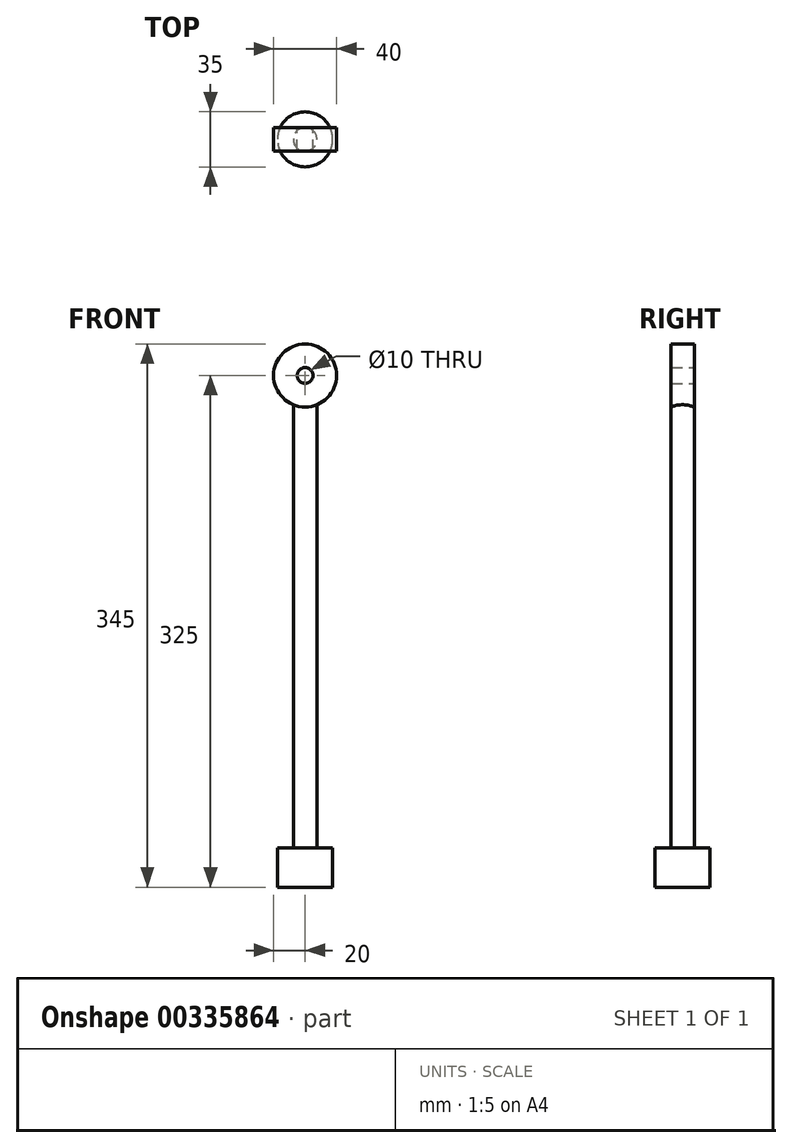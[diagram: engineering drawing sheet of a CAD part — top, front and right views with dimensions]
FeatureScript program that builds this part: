
annotation { "Feature Type Name" : "Feature", "Feature Type Description" : "" }
export const myFeature = defineFeature(function(context is Context, id is Id, definition is map)
    precondition{}
    {
        {
            var Q0;
            Q0=qCreatedBy(makeId("Front.planeOp"),FACE);
            var sketch = newSketch(context, id + "F0", { "sketchPlane" : qUnion([Q0])});
            skCircle(sketch, "E0", {"center": v(0, 0) * mm, "radius": 20 * mm});
            skCircle(sketch, "E1", {"center": v(0, 0) * mm, "radius": 5 * mm});
            skSolve(sketch);
        }
        {
            var Q0;
            Q0=makeQuery(id+"F0.imprint","IMPRINT",FACE,{"disambiguationData":[TD([[makeQuery(id+"F0.imprint","IMPRINT",EDGE,{"derivedFrom":sQuery(id+"F0.wireOp",EDGE,"E0")}),1.0]])]});
            extrude(context, id + "F1", {"entities" : qUnion([Q0]), "depth" : 15 * mm, "symmetric" : true});
        }
        {
            var Q0;
            Q0=qCreatedBy(makeId("Top.planeOp"),FACE);
            cPlane(context, id + "F2", {"entities" : qUnion([Q0]), "cplaneType" : CPlaneType.OFFSET, "offset" : 300 * mm, "oppositeDirection" : true, "width" : 150 * mm, "height" : 150 * mm});
        }
        {
            var Q0;
            Q0=qCreatedBy(id+"F2.planeOp",FACE);
            var sketch = newSketch(context, id + "F3", { "sketchPlane" : qUnion([Q0])});
            skCircle(sketch, "E2", {"center": v(0, 0) * mm, "radius": 7.5 * mm});
            skSolve(sketch);
        }
        {
            var Q0;
            Q0=makeQuery(id+"F3.imprint","IMPRINT",FACE,{"disambiguationData":[TD([[makeQuery(id+"F3.imprint","IMPRINT",EDGE,{"derivedFrom":sQuery(id+"F3.wireOp",EDGE,"E2")}),1.0]])]});
            extrude(context, id + "F4", {"entities" : qUnion([Q0]), "operationType" : NewBodyOperationType.ADD, "endBound" : BoundingType.UP_TO_NEXT, "depth" : 25 * mm});
        }
        {
            var Q0;
            Q0=qCreatedBy(id+"F2.planeOp",FACE);
            var sketch = newSketch(context, id + "F5", { "sketchPlane" : qUnion([Q0])});
            skCircle(sketch, "E3", {"center": v(0, 0) * mm, "radius": 17.5 * mm});
            skSolve(sketch);
        }
        {
            var Q0;
            Q0=makeQuery(id+"F5.imprint","IMPRINT",FACE,{"disambiguationData":[TD([[makeQuery(id+"F5.imprint","IMPRINT",EDGE,{"derivedFrom":sQuery(id+"F5.wireOp",EDGE,"E3")}),1.0]])]});
            extrude(context, id + "F6", {"entities" : qUnion([Q0]), "operationType" : NewBodyOperationType.ADD, "oppositeDirection" : true, "depth" : 25 * mm});
        }
    });
